# Revit family: Tub_Spout-GROHE-Atrio-13488_Series
name_source: partatom
category: Plumbing Fixtures
units: mm (PartAtom-declared; Revit-internal decimal feet)

## family parameters
Cut with Voids When Loaded = No
Host = Face
OmniClass Number = 23.45.05.14.21.11
OmniClass Title = Bath/Shower Units
Part Type = Normal
Room Calculation Point = No
Round Connector Dimension = Use Diameter
Shared = Yes

## types (4) — shared parameters
Assembly Code = D2010510
CW Connection = No
CWFU = 3
Default Elevation = 24"
Description = Atrio Tub Spout
HW Connection = No
HWFU = 3
IAPMO Compliance = • Massachusetts Plumbing Board Approved  • CSA B125.1 • ASME A112.18.1
Installation Type = Wall Mounted
Manufacturer = Grohe
Plate Thickness = 2 9/16"
Price = Prices may vary. Please consult Manufacturer Representative for most up-to-date price list.
Product Page URL = https://www.grohe.us
Spout Reach = 6 3/4"
Tempered Connection = Yes
Tempered Water Connection Diameter = 1/2"
URL = https://www.grohe.us
Vent Connection = No
WFU = 4
Waste Connection = No
Width = 2 9/16"

## per-type parameters (varying)
| type | Finish | Material |
| 13488000 | Metal-Grohe-000-StarLight Chrome | Metal-Grohe-000-StarLight Chrome |
| 134882430 | Metal-Grohe-2430-Matte Black | Metal-Grohe-2430-Matte Black |
| 13488EN0 | Metal-Grohe-EN0-Brushed Nickel Infinity Finish | Metal-Grohe-EN0-Brushed Nickel Infinity Finish |
| 13488GN0 | Metal-Grohe-GN0-Brushed Cool Sunrise | Metal-Grohe-GN0-Brushed Cool Sunrise |

note: column(s) folded — value = type name in every type: Model

## geometry (parser evidence)
native form markers: Sweep x3
no freeform markers — native parametric forms only
